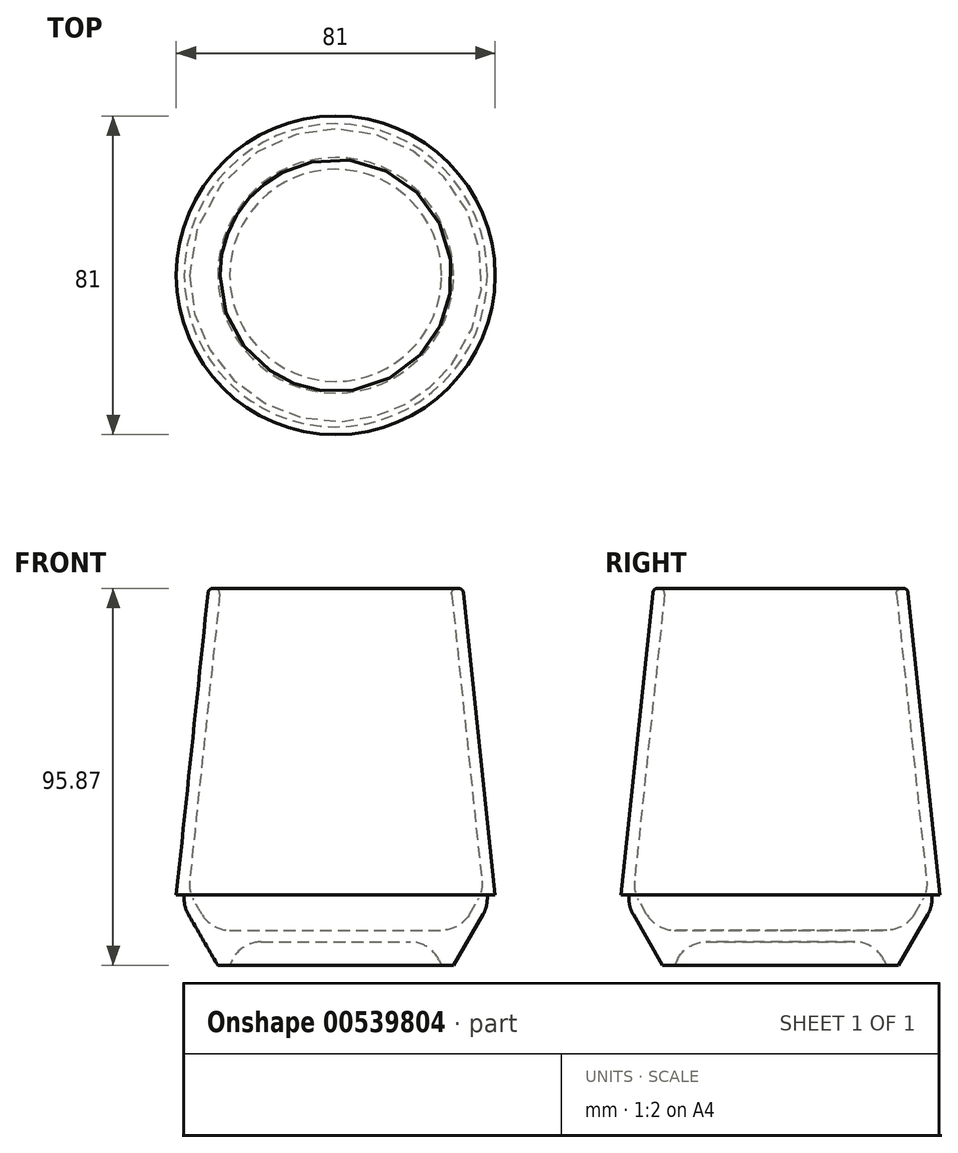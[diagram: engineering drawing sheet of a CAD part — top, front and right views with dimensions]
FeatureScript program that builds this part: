
annotation { "Feature Type Name" : "Feature", "Feature Type Description" : "" }
export const myFeature = defineFeature(function(context is Context, id is Id, definition is map)
    precondition{}
    {
        {
            var Q0;
            Q0=qCreatedBy(makeId("Front.planeOp"),FACE);
            var sketch = newSketch(context, id + "F0", { "sketchPlane" : qUnion([Q0])});
            skLineSegment(sketch, "E0", {"start": v(0, 6) * mm, "end": v(18.96, 6) * mm});
            skLineSegment(sketch, "E1", {"start": v(26.22, 1.47) * mm, "end": v(26.94, 0) * mm});
            skLineSegment(sketch, "E2", {"start": v(26.94, 0) * mm, "end": v(29.94, 0) * mm});
            skLineSegment(sketch, "E3", {"start": v(29.94, 0) * mm, "end": v(37.42, 12.96) * mm});
            skLineSegment(sketch, "E4", {"start": v(38.5, 17) * mm, "end": v(38.5, 18) * mm});
            skLineSegment(sketch, "E5", {"start": v(38.5, 18) * mm, "end": v(40.5, 18) * mm});
            skLineSegment(sketch, "E6", {"start": v(40.5, 18) * mm, "end": v(32.44, 94.7) * mm});
            skLineSegment(sketch, "E7", {"start": v(31, 95.86) * mm, "end": v(30.61, 95.82) * mm});
            skLineSegment(sketch, "E8", {"start": v(29.45, 94.4) * mm, "end": v(37.11, 21.52) * mm});
            skLineSegment(sketch, "E9", {"start": v(36.07, 16.63) * mm, "end": v(34, 13.04) * mm});
            skLineSegment(sketch, "E10", {"start": v(27, 9) * mm, "end": v(0, 9) * mm});
            skLineSegment(sketch, "E11", {"start": v(0, 9) * mm, "end": v(0, 6) * mm});
            skPoint(sketch, "E12.visualSharp", {"position": v(24, 6) * mm});
            skArc(sketch, "E12.filletArc", {"start": v(26.22, 1.47) * mm, "mid": v(23.24, 4.77) * mm, "end": v(18.96, 6) * mm});
            skPoint(sketch, "E13.visualSharp", {"position": v(31.67, 9) * mm});
            skArc(sketch, "E13.filletArc", {"start": v(27, 9) * mm, "mid": v(31.04, 10.08) * mm, "end": v(34, 13.04) * mm});
            skPoint(sketch, "E14.visualSharp", {"position": v(37.39, 18.9) * mm});
            skArc(sketch, "E14.filletArc", {"start": v(36.07, 16.63) * mm, "mid": v(36.98, 19) * mm, "end": v(37.11, 21.52) * mm});
            skPoint(sketch, "E15.visualSharp", {"position": v(38.5, 14.83) * mm});
            skArc(sketch, "E15.filletArc", {"start": v(37.42, 12.96) * mm, "mid": v(38.22, 14.9) * mm, "end": v(38.5, 17) * mm});
            skPoint(sketch, "E16.visualSharp", {"position": v(32.3, 96) * mm});
            skArc(sketch, "E16.filletArc", {"start": v(32.44, 94.7) * mm, "mid": v(31.96, 95.58) * mm, "end": v(31, 95.86) * mm});
            skPoint(sketch, "E17.visualSharp", {"position": v(29.32, 95.69) * mm});
            skArc(sketch, "E17.filletArc", {"start": v(30.61, 95.82) * mm, "mid": v(29.74, 95.35) * mm, "end": v(29.45, 94.4) * mm});
            skLineSegment(sketch, "E18", {"start": v(40.5, 18) * mm, "end": v(40.5, 96) * mm, "construction": true});
            skLineSegment(sketch, "E19", {"start": v(0, 0) * mm, "end": v(0, 94.7) * mm, "construction": true});
            skSolve(sketch);
        }
        {
            var Q0;
            Q0=qSketchRegion(id+"F0",true);
            var Q1;
            Q1=sQuery(id+"F0.wireOp",EDGE,"E19");
            revolve(context, id + "F1", {"entities" : qUnion([Q0]), "axis" : qUnion([Q1]), "revolveType" : RevolveType.FULL});
        }
    });
